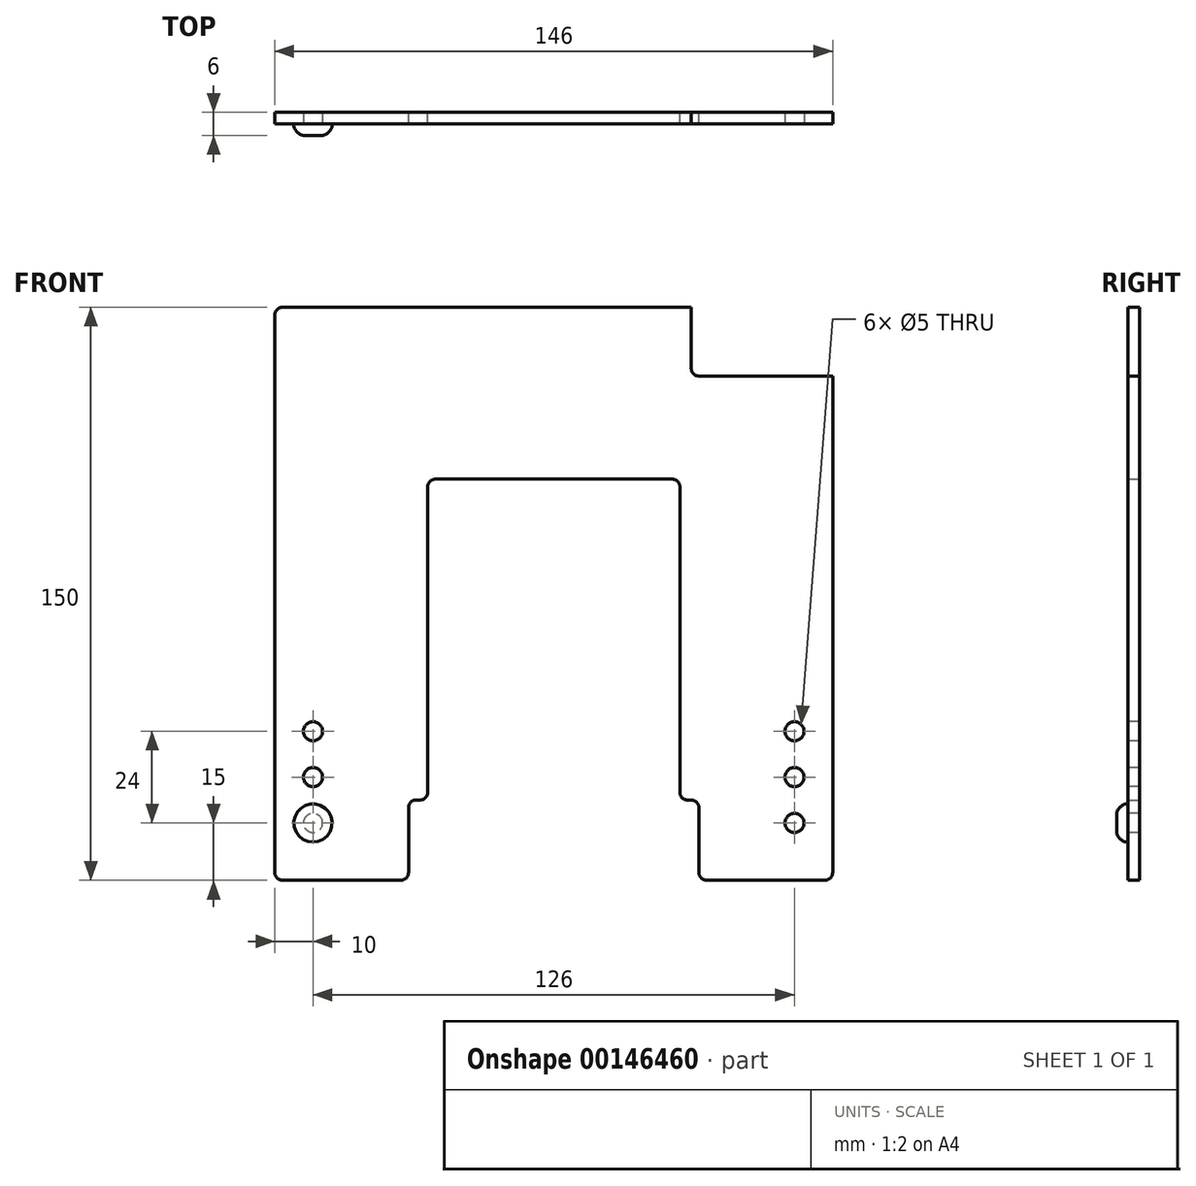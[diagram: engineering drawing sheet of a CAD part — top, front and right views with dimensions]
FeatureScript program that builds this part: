
annotation { "Feature Type Name" : "Feature", "Feature Type Description" : "" }
export const myFeature = defineFeature(function(context is Context, id is Id, definition is map)
    precondition{}
    {
        {
            var Q0;
            Q0=qCreatedBy(makeId("Front.planeOp"),FACE);
            var sketch = newSketch(context, id + "F0", { "sketchPlane" : qUnion([Q0])});
            skLineSegment(sketch, "E0", {"start": v(-73, 0) * mm, "end": v(-38, 0) * mm});
            skLineSegment(sketch, "E1", {"start": v(-38, 0) * mm, "end": v(-38, 21) * mm});
            skLineSegment(sketch, "E2", {"start": v(-38, 21) * mm, "end": v(-33, 21) * mm});
            skLineSegment(sketch, "E3", {"start": v(-33, 21) * mm, "end": v(-33, 105) * mm});
            skLineSegment(sketch, "E4", {"start": v(-33, 105) * mm, "end": v(0, 105) * mm});
            skLineSegment(sketch, "E5", {"start": v(0, 105) * mm, "end": v(0, 150) * mm});
            skLineSegment(sketch, "E6", {"start": v(0, 150) * mm, "end": v(-73, 150) * mm});
            skLineSegment(sketch, "E7", {"start": v(-73, 150) * mm, "end": v(-73, 0) * mm});
            skSolve(sketch);
        }
        {
            var Q0;
            Q0 = qSketchRegion(id + "F0", true);
            extrude(context, id + "F1", {"entities" : qUnion([Q0]), "depth" : 3 * mm, "symmetric" : true});
        }
        {
            var Q0;
            Q0=makeQuery(id+"F1.opExtrude","SWEPT_BODY",BODY,{"disambiguationData":[OSD([sQuery(id+"F0.wireOp",EDGE,"E0"),sQuery(id+"F0.wireOp",EDGE,"E1"),sQuery(id+"F0.wireOp",EDGE,"E2"),sQuery(id+"F0.wireOp",EDGE,"E3"),sQuery(id+"F0.wireOp",EDGE,"E4"),sQuery(id+"F0.wireOp",EDGE,"E5"),sQuery(id+"F0.wireOp",EDGE,"E6"),sQuery(id+"F0.wireOp",EDGE,"E7")])]});
            var Q1;
            Q1=makeQuery(id+"F1.opExtrude","SWEPT_FACE",FACE,{"disambiguationData":[OSD([sQuery(id+"F0.wireOp",EDGE,"E5")])]});
            mirror(context, id + "F2", {"operationType" : NewBodyOperationType.ADD, "entities" : qUnion([Q0]), "mirrorPlane" : qUnion([Q1])});
        }
        {
            var Q0;
            {var subQ0=makeQuery(id+"F1.opExtrude","CAP_FACE",FACE,{"disambiguationData":[OSD([sQuery(id+"F0.wireOp",EDGE,"E0"),sQuery(id+"F0.wireOp",EDGE,"E1"),sQuery(id+"F0.wireOp",EDGE,"E2"),sQuery(id+"F0.wireOp",EDGE,"E3"),sQuery(id+"F0.wireOp",EDGE,"E4"),sQuery(id+"F0.wireOp",EDGE,"E5"),sQuery(id+"F0.wireOp",EDGE,"E6"),sQuery(id+"F0.wireOp",EDGE,"E7")])],"isStart":false});Q0=makeQuery(id+"F2.boolean.opBoolean","MERGE",FACE,{"derivedFrom":[subQ0,makeQuery(id+"F2.opPattern","COPY",FACE,{"derivedFrom":subQ0,"instanceName":"1"})]});}
            var sketch = newSketch(context, id + "F3", { "sketchPlane" : qUnion([Q0])});
            skLineSegment(sketch, "E8.bottom", {"start": v(73, 150) * mm, "end": v(36, 150) * mm});
            skLineSegment(sketch, "E8.top", {"start": v(73, 132) * mm, "end": v(36, 132) * mm});
            skLineSegment(sketch, "E8.left", {"start": v(73, 150) * mm, "end": v(73, 132) * mm});
            skLineSegment(sketch, "E8.right", {"start": v(36, 150) * mm, "end": v(36, 132) * mm});
            skSolve(sketch);
        }
        {
            var Q0;
            Q0 = qSketchRegion(id + "F3", true);
            extrude(context, id + "F4", {"entities" : qUnion([Q0]), "operationType" : NewBodyOperationType.REMOVE, "endBound" : BoundingType.THROUGH_ALL, "oppositeDirection" : true, "depth" : 25 * mm});
        }
        {
            var Q0;
            Q0=makeQuery(id+"F4.boolean.opBoolean","COPY",EDGE,{"derivedFrom":makeQuery(id+"F4.opExtrude","SWEPT_EDGE",EDGE,{"disambiguationData":[OSD([sQuery(id+"F0.wireOp",EDGE,"E6"),sQuery(id+"F3.wireOp",EDGE,"E8.bottom"),sQuery(id+"F3.wireOp",EDGE,"E8.right")])]})});
            var Q1;
            Q1=makeQuery(id+"F4.boolean.opBoolean","COPY",EDGE,{"derivedFrom":makeQuery(id+"F4.opExtrude","SWEPT_EDGE",EDGE,{"disambiguationData":[OSD([sQuery(id+"F3.wireOp",EDGE,"E8.top"),sQuery(id+"F3.wireOp",EDGE,"E8.right")])]})});
            var Q2;
            Q2=makeQuery(id+"F4.boolean.opBoolean","COPY",EDGE,{"derivedFrom":makeQuery(id+"F4.opExtrude","SWEPT_EDGE",EDGE,{"disambiguationData":[OSD([sQuery(id+"F0.wireOp",EDGE,"E7"),sQuery(id+"F3.wireOp",EDGE,"E8.top"),sQuery(id+"F3.wireOp",EDGE,"E8.left")])]})});
            var Q3;
            Q3=makeQuery(id+"F1.opExtrude","SWEPT_EDGE",EDGE,{"disambiguationData":[OSD([sQuery(id+"F0.wireOp",EDGE,"E6"),sQuery(id+"F0.wireOp",EDGE,"E7")])]});
            var Q4;
            Q4=makeQuery(id+"F1.opExtrude","SWEPT_EDGE",EDGE,{"disambiguationData":[OSD([sQuery(id+"F0.wireOp",EDGE,"E0"),sQuery(id+"F0.wireOp",EDGE,"E1")])]});
            var Q5;
            Q5=makeQuery(id+"F1.opExtrude","SWEPT_EDGE",EDGE,{"disambiguationData":[OSD([sQuery(id+"F0.wireOp",EDGE,"E2"),sQuery(id+"F0.wireOp",EDGE,"E3")])]});
            var Q6;
            Q6=makeQuery(id+"F2.opPattern","COPY",EDGE,{"derivedFrom":makeQuery(id+"F1.opExtrude","SWEPT_EDGE",EDGE,{"disambiguationData":[OSD([sQuery(id+"F0.wireOp",EDGE,"E0"),sQuery(id+"F0.wireOp",EDGE,"E7")])]}),"instanceName":"1"});
            var Q7;
            Q7=makeQuery(id+"F2.opPattern","COPY",EDGE,{"derivedFrom":makeQuery(id+"F1.opExtrude","SWEPT_EDGE",EDGE,{"disambiguationData":[OSD([sQuery(id+"F0.wireOp",EDGE,"E2"),sQuery(id+"F0.wireOp",EDGE,"E3")])]}),"instanceName":"1"});
            var Q8;
            Q8=makeQuery(id+"F2.opPattern","COPY",EDGE,{"derivedFrom":makeQuery(id+"F1.opExtrude","SWEPT_EDGE",EDGE,{"disambiguationData":[OSD([sQuery(id+"F0.wireOp",EDGE,"E1"),sQuery(id+"F0.wireOp",EDGE,"E2")])]}),"instanceName":"1"});
            var Q9;
            Q9=makeQuery(id+"F2.opPattern","COPY",EDGE,{"derivedFrom":makeQuery(id+"F1.opExtrude","SWEPT_EDGE",EDGE,{"disambiguationData":[OSD([sQuery(id+"F0.wireOp",EDGE,"E0"),sQuery(id+"F0.wireOp",EDGE,"E1")])]}),"instanceName":"1"});
            var Q10;
            Q10=makeQuery(id+"F1.opExtrude","SWEPT_EDGE",EDGE,{"disambiguationData":[OSD([sQuery(id+"F0.wireOp",EDGE,"E1"),sQuery(id+"F0.wireOp",EDGE,"E2")])]});
            var Q11;
            Q11=makeQuery(id+"F1.opExtrude","SWEPT_EDGE",EDGE,{"disambiguationData":[OSD([sQuery(id+"F0.wireOp",EDGE,"E0"),sQuery(id+"F0.wireOp",EDGE,"E7")])]});
            var Q12;
            Q12=makeQuery(id+"F1.opExtrude","SWEPT_EDGE",EDGE,{"disambiguationData":[OSD([sQuery(id+"F0.wireOp",EDGE,"E3"),sQuery(id+"F0.wireOp",EDGE,"E4")])]});
            var Q13;
            Q13=makeQuery(id+"F2.opPattern","COPY",EDGE,{"derivedFrom":makeQuery(id+"F1.opExtrude","SWEPT_EDGE",EDGE,{"disambiguationData":[OSD([sQuery(id+"F0.wireOp",EDGE,"E3"),sQuery(id+"F0.wireOp",EDGE,"E4")])]}),"instanceName":"1"});
            fillet(context, id + "F5", {"entities" : qUnion([Q0, Q1, Q2, Q3, Q4, Q5, Q6, Q7, Q8, Q9, Q10, Q11, Q12, Q13]), "radius" : 2 * mm, "tangentPropagation" : true, "allowEdgeOverflow" : false});
        }
        {
            var Q0;
            {var subQ0=makeQuery(id+"F1.opExtrude","CAP_FACE",FACE,{"disambiguationData":[OSD([sQuery(id+"F0.wireOp",EDGE,"E0"),sQuery(id+"F0.wireOp",EDGE,"E1"),sQuery(id+"F0.wireOp",EDGE,"E2"),sQuery(id+"F0.wireOp",EDGE,"E3"),sQuery(id+"F0.wireOp",EDGE,"E4"),sQuery(id+"F0.wireOp",EDGE,"E5"),sQuery(id+"F0.wireOp",EDGE,"E6"),sQuery(id+"F0.wireOp",EDGE,"E7")])],"isStart":false});Q0=makeQuery(id+"F2.boolean.opBoolean","MERGE",FACE,{"derivedFrom":[subQ0,makeQuery(id+"F2.opPattern","COPY",FACE,{"derivedFrom":subQ0,"instanceName":"1"})]});}
            var sketch = newSketch(context, id + "F6", { "sketchPlane" : qUnion([Q0])});
            skCircle(sketch, "E9", {"center": v(-63, 15) * mm, "radius": 2.5 * mm});
            skCircle(sketch, "E10.0.1.0", {"center": v(-63, 27) * mm, "radius": 2.5 * mm});
            skCircle(sketch, "E10.0.2.0", {"center": v(-63, 39) * mm, "radius": 2.5 * mm});
            skCircle(sketch, "E10.1.0.0", {"center": v(63, 15) * mm, "radius": 2.5 * mm});
            skCircle(sketch, "E10.1.1.0", {"center": v(63, 27) * mm, "radius": 2.5 * mm});
            skCircle(sketch, "E10.1.2.0", {"center": v(63, 39) * mm, "radius": 2.5 * mm});
            skLineSegment(sketch, "E10.direction1", {"start": v(-63, 15) * mm, "end": v(60.5, 15) * mm, "construction": true});
            skLineSegment(sketch, "E10.direction2", {"start": v(-63, 15) * mm, "end": v(-63, 27) * mm, "construction": true});
            skSolve(sketch);
        }
        {
            var Q0;
            Q0 = qSketchRegion(id + "F6", true);
            extrude(context, id + "F7", {"entities" : qUnion([Q0]), "operationType" : NewBodyOperationType.REMOVE, "endBound" : BoundingType.THROUGH_ALL, "oppositeDirection" : true, "depth" : 25 * mm});
        }
        {
            var Q0;
            {var subQ0=makeQuery(id+"F1.opExtrude","CAP_FACE",FACE,{"disambiguationData":[OSD([sQuery(id+"F0.wireOp",EDGE,"E0"),sQuery(id+"F0.wireOp",EDGE,"E1"),sQuery(id+"F0.wireOp",EDGE,"E2"),sQuery(id+"F0.wireOp",EDGE,"E3"),sQuery(id+"F0.wireOp",EDGE,"E4"),sQuery(id+"F0.wireOp",EDGE,"E5"),sQuery(id+"F0.wireOp",EDGE,"E6"),sQuery(id+"F0.wireOp",EDGE,"E7")])],"isStart":false});Q0=makeQuery(id+"F2.boolean.opBoolean","MERGE",FACE,{"derivedFrom":[subQ0,makeQuery(id+"F2.opPattern","COPY",FACE,{"derivedFrom":subQ0,"instanceName":"1"})]});}
            var sketch = newSketch(context, id + "F8", { "sketchPlane" : qUnion([Q0])});
            skCircle(sketch, "E11", {"center": v(-63, 15) * mm, "radius": 5 * mm});
            skSolve(sketch);
        }
        {
            var Q0;
            Q0 = qSketchRegion(id + "F8", true);
            extrude(context, id + "F9", {"entities" : qUnion([Q0]), "depth" : 3 * mm});
        }
        {
            var Q0;
            Q0=makeQuery(id+"F9.opExtrude","CAP_EDGE",EDGE,{"disambiguationData":[OSD([sQuery(id+"F8.wireOp",EDGE,"E11")])],"isStart":false});
            fillet(context, id + "F10", {"entities" : qUnion([Q0]), "radius" : 2.5 * mm, "rho" : 0.3, "crossSection" : FilletCrossSection.CONIC, "allowEdgeOverflow" : false});
        }
    });
